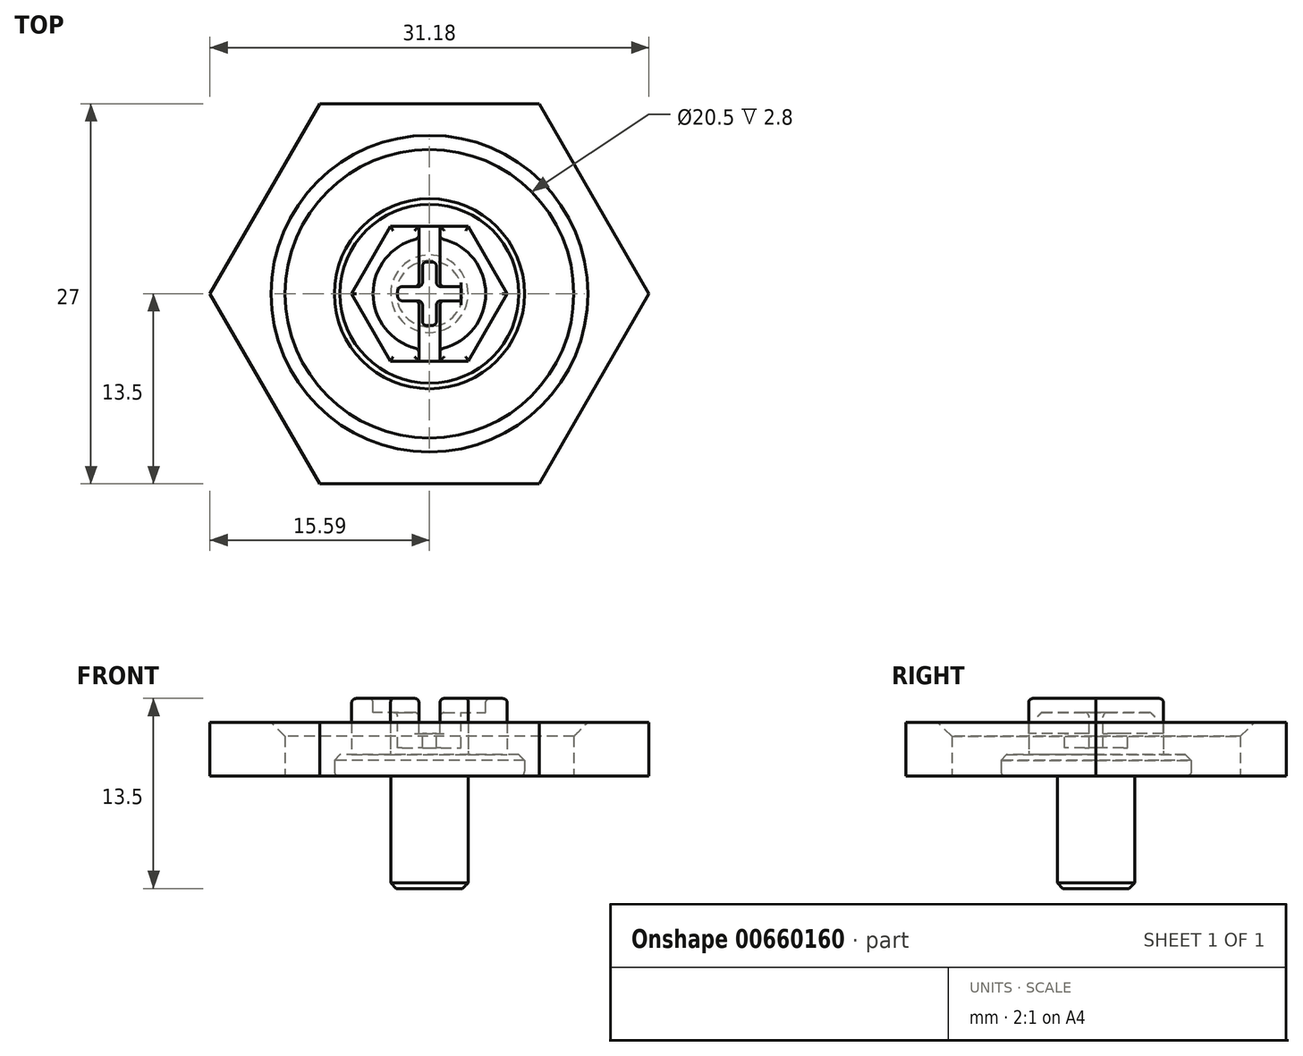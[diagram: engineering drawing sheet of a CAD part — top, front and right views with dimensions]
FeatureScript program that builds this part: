
annotation { "Feature Type Name" : "Feature", "Feature Type Description" : "" }
export const myFeature = defineFeature(function(context is Context, id is Id, definition is map)
    precondition{}
    {
        {
            var Q0;
            Q0=qCreatedBy(makeId("Top.planeOp"),FACE);
            var sketch = newSketch(context, id + "F0", { "sketchPlane" : qUnion([Q0])});
            skCircle(sketch, "E0.cCircle", {"center": v(0, 0) * mm, "radius": 13.5 * mm, "construction": true});
            skLineSegment(sketch, "E0.0", {"start": v(-7.8, 13.5) * mm, "end": v(7.8, 13.5) * mm});
            skLineSegment(sketch, "E0.1", {"start": v(7.8, 13.5) * mm, "end": v(15.59, 0) * mm});
            skLineSegment(sketch, "E0.2", {"start": v(15.59, 0) * mm, "end": v(7.8, -13.5) * mm});
            skLineSegment(sketch, "E0.3", {"start": v(7.8, -13.5) * mm, "end": v(-7.8, -13.5) * mm});
            skLineSegment(sketch, "E0.4", {"start": v(-7.8, -13.5) * mm, "end": v(-15.59, 0) * mm});
            skLineSegment(sketch, "E0.5", {"start": v(-15.59, 0) * mm, "end": v(-7.8, 13.5) * mm});
            skPoint(sketch, "E0.0.midPoint", {"position": v(0, 13.5) * mm});
            skCircle(sketch, "E1", {"center": v(0, 0) * mm, "radius": 10.25 * mm});
            skSolve(sketch);
        }
        {
            var Q0;
            Q0=makeQuery(id+"F0.imprint","IMPRINT",FACE,{"disambiguationData":[TD([[makeQuery(id+"F0.imprint","IMPRINT",EDGE,{"derivedFrom":sQuery(id+"F0.wireOp",EDGE,"E0.0")}),-1.0]])]});
            extrude(context, id + "F1", {"entities" : qUnion([Q0]), "depth" : 3.8 * mm});
        }
        {
            var Q0;
            Q0=makeQuery(id+"F1.opExtrude","CAP_EDGE",EDGE,{"disambiguationData":[OSD([sQuery(id+"F0.wireOp",EDGE,"E1")])],"isStart":false});
            chamfer(context, id + "F2", {"entities" : qUnion([Q0]), "width" : 1 * mm, "tangentPropagation" : true});
        }
        {
            var Q0;
            Q0=qCreatedBy(makeId("Top.planeOp"),FACE);
            var sketch = newSketch(context, id + "F3", { "sketchPlane" : qUnion([Q0])});
            skCircle(sketch, "E2", {"center": v(0, 0) * mm, "radius": 6.75 * mm});
            skCircle(sketch, "E3", {"center": v(0, 0) * mm, "radius": 2.75 * mm});
            skSolve(sketch);
        }
        {
            var Q0;
            Q0=makeQuery(id+"F3.imprint","IMPRINT",FACE,{"disambiguationData":[TD([[makeQuery(id+"F3.imprint","IMPRINT",EDGE,{"derivedFrom":sQuery(id+"F3.wireOp",EDGE,"E3")}),1.0]])]});
            extrude(context, id + "F4", {"entities" : qUnion([Q0]), "oppositeDirection" : true, "depth" : 8 * mm});
        }
        {
            var Q0;
            Q0=makeQuery(id+"F3.imprint","IMPRINT",FACE,{"disambiguationData":[TD([[makeQuery(id+"F3.imprint","IMPRINT",EDGE,{"derivedFrom":sQuery(id+"F3.wireOp",EDGE,"E2")}),1.0]])]});
            var Q1;
            Q1=makeQuery(id+"F3.imprint","IMPRINT",FACE,{"disambiguationData":[TD([[makeQuery(id+"F3.imprint","IMPRINT",EDGE,{"derivedFrom":sQuery(id+"F3.wireOp",EDGE,"E3")}),1.0]])]});
            extrude(context, id + "F5", {"entities" : qUnion([Q0, Q1]), "operationType" : NewBodyOperationType.ADD, "depth" : 1.5 * mm});
        }
        {
            var Q0;
            Q0=makeQuery(id+"F5.opExtrude","CAP_FACE",FACE,{"disambiguationData":[OSD([sQuery(id+"F3.wireOp",EDGE,"E2")])],"isStart":false});
            var sketch = newSketch(context, id + "F6", { "sketchPlane" : qUnion([Q0])});
            skCircle(sketch, "E4.cCircle", {"center": v(0, 0) * mm, "radius": 4.78 * mm, "construction": true});
            skLineSegment(sketch, "E4.0", {"start": v(-2.76, 4.78) * mm, "end": v(2.76, 4.78) * mm});
            skLineSegment(sketch, "E4.1", {"start": v(2.76, 4.78) * mm, "end": v(5.53, 0) * mm});
            skLineSegment(sketch, "E4.2", {"start": v(5.53, 0) * mm, "end": v(2.76, -4.78) * mm});
            skLineSegment(sketch, "E4.3", {"start": v(2.76, -4.78) * mm, "end": v(-2.76, -4.78) * mm});
            skLineSegment(sketch, "E4.4", {"start": v(-2.76, -4.78) * mm, "end": v(-5.53, 0) * mm});
            skLineSegment(sketch, "E4.5", {"start": v(-5.53, 0) * mm, "end": v(-2.76, 4.78) * mm});
            skPoint(sketch, "E4.0.midPoint", {"position": v(0, 4.78) * mm});
            skSolve(sketch);
        }
        {
            var Q0;
            Q0=makeQuery(id+"F6.imprint","IMPRINT",FACE,{"disambiguationData":[TD([[makeQuery(id+"F6.imprint","IMPRINT",EDGE,{"derivedFrom":sQuery(id+"F6.wireOp",EDGE,"E4.0")}),-1.0]])]});
            extrude(context, id + "F7", {"entities" : qUnion([Q0]), "operationType" : NewBodyOperationType.ADD, "depth" : 4 * mm});
        }
        {
            var Q0;
            Q0=makeQuery(id+"F7.opExtrude","CAP_FACE",FACE,{"disambiguationData":[OSD([sQuery(id+"F6.wireOp",EDGE,"E4.0"),sQuery(id+"F6.wireOp",EDGE,"E4.1"),sQuery(id+"F6.wireOp",EDGE,"E4.2"),sQuery(id+"F6.wireOp",EDGE,"E4.3"),sQuery(id+"F6.wireOp",EDGE,"E4.4"),sQuery(id+"F6.wireOp",EDGE,"E4.5")])],"isStart":false});
            var sketch = newSketch(context, id + "F8", { "sketchPlane" : qUnion([Q0])});
            skCircle(sketch, "E5", {"center": v(0, 0) * mm, "radius": 4 * mm});
            skSolve(sketch);
        }
        {
            var Q0;
            Q0=makeQuery(id+"F8.imprint","IMPRINT",FACE,{"disambiguationData":[TD([[makeQuery(id+"F8.imprint","IMPRINT",EDGE,{"derivedFrom":sQuery(id+"F8.wireOp",EDGE,"E5")}),1.0]])]});
            extrude(context, id + "F9", {"entities" : qUnion([Q0]), "operationType" : NewBodyOperationType.REMOVE, "oppositeDirection" : true, "depth" : 1 * mm});
        }
        {
            var Q0;
            Q0=makeQuery(id+"F7.opExtrude","CAP_FACE",FACE,{"disambiguationData":[OSD([sQuery(id+"F6.wireOp",EDGE,"E4.0"),sQuery(id+"F6.wireOp",EDGE,"E4.1"),sQuery(id+"F6.wireOp",EDGE,"E4.2"),sQuery(id+"F6.wireOp",EDGE,"E4.3"),sQuery(id+"F6.wireOp",EDGE,"E4.4"),sQuery(id+"F6.wireOp",EDGE,"E4.5")])],"isStart":false});
            var sketch = newSketch(context, id + "F10", { "sketchPlane" : qUnion([Q0])});
            skLineSegment(sketch, "E6.bottom", {"start": v(-0.75, 5) * mm, "end": v(0.75, 5) * mm});
            skLineSegment(sketch, "E6.top", {"start": v(-0.75, -5) * mm, "end": v(0.75, -5) * mm});
            skLineSegment(sketch, "E6.left", {"start": v(-0.75, 5) * mm, "end": v(-0.75, -5) * mm});
            skLineSegment(sketch, "E6.right", {"start": v(0.75, 5) * mm, "end": v(0.75, -5) * mm});
            skPoint(sketch, "E6.middle", {"position": v(0, 0) * mm});
            skSolve(sketch);
        }
        {
            var Q0;
            {var subQ0=sQuery(id+"F10.wireOp",EDGE,"E6.left");var subQ1=makeQuery(id+"F7.opExtrude","CAP_EDGE",EDGE,{"disambiguationData":[OSD([sQuery(id+"F6.wireOp",EDGE,"E4.0")])],"isStart":false});var subQ2=makeQuery(id+"F10.imprint","INTERSECT",VERTEX,{"derivedFrom":[subQ1,subQ0]});Q0=makeQuery(id+"F10.imprint","IMPRINT",FACE,{"disambiguationData":[TD([[makeQuery(id+"F10.imprint","IMPRINT",EDGE,{"disambiguationData":[TD([[subQ2,-1.0]])],"derivedFrom":subQ0}),1.0]])]});}
            var Q1;
            {var subQ0=sQuery(id+"F10.wireOp",EDGE,"E6.left");var subQ1=makeQuery(id+"F9.boolean.opBoolean","COPY",EDGE,{"derivedFrom":makeQuery(id+"F9.opExtrude","CAP_EDGE",EDGE,{"disambiguationData":[OSD([sQuery(id+"F8.wireOp",EDGE,"E5")])],"isStart":true})});var subQ2=makeQuery(id+"F10.imprint","INTERSECT",VERTEX,{"disambiguationData":[OD(0.0)],"derivedFrom":[subQ1,subQ0]});Q1=makeQuery(id+"F10.imprint","IMPRINT",FACE,{"disambiguationData":[TD([[makeQuery(id+"F10.imprint","IMPRINT",EDGE,{"disambiguationData":[TD([[subQ2,-1.0]])],"derivedFrom":subQ0}),1.0]])]});}
            var Q2;
            {var subQ0=sQuery(id+"F10.wireOp",EDGE,"E6.left");var subQ1=makeQuery(id+"F7.opExtrude","CAP_EDGE",EDGE,{"disambiguationData":[OSD([sQuery(id+"F6.wireOp",EDGE,"E4.3")])],"isStart":false});var subQ2=makeQuery(id+"F10.imprint","INTERSECT",VERTEX,{"derivedFrom":[subQ1,subQ0]});Q2=makeQuery(id+"F10.imprint","IMPRINT",FACE,{"disambiguationData":[TD([[makeQuery(id+"F10.imprint","IMPRINT",EDGE,{"disambiguationData":[TD([[subQ2,1.0]])],"derivedFrom":subQ0}),1.0]])]});}
            var Q3;
            Q3=makeQuery(id+"F5.opExtrude","CAP_FACE",FACE,{"disambiguationData":[OSD([sQuery(id+"F3.wireOp",EDGE,"E2")])],"isStart":false});
            extrude(context, id + "F11", {"entities" : qUnion([Q0, Q1, Q2]), "operationType" : NewBodyOperationType.REMOVE, "oppositeDirection" : true, "endBoundEntityFace" : qUnion([Q3]), "depth" : 2.5 * mm});
        }
        {
            var Q0;
            {var subQ0=sQuery(id+"F8.wireOp",EDGE,"E5");Q0=makeQuery(id+"F11.boolean.opBoolean","SPLIT",FACE,{"disambiguationData":[TD([makeQuery(id+"F11.opExtrude","SWEPT_FACE",FACE,{"disambiguationData":[OSD([sQuery(id+"F10.wireOp",EDGE,"E6.left")])]})])],"derivedFrom":makeQuery(id+"F9.boolean.opBoolean","COPY",FACE,{"derivedFrom":makeQuery(id+"F9.opExtrude","CAP_FACE",FACE,{"disambiguationData":[OSD([subQ0])],"isStart":false})})});}
            var sketch = newSketch(context, id + "F12", { "sketchPlane" : qUnion([Q0])});
            skLineSegment(sketch, "E7.bottom", {"start": v(-0.5, 2.25) * mm, "end": v(0.5, 2.25) * mm});
            skLineSegment(sketch, "E7.top", {"start": v(-0.5, -2.25) * mm, "end": v(0.5, -2.25) * mm});
            skLineSegment(sketch, "E7.left", {"start": v(-0.5, 2.25) * mm, "end": v(-0.5, -2.25) * mm});
            skLineSegment(sketch, "E7.right", {"start": v(0.5, 2.25) * mm, "end": v(0.5, -2.25) * mm});
            skPoint(sketch, "E7.middle", {"position": v(0, 0) * mm});
            skLineSegment(sketch, "E8.bottom", {"start": v(-2.25, 0.5) * mm, "end": v(2.25, 0.5) * mm});
            skLineSegment(sketch, "E8.top", {"start": v(-2.25, -0.5) * mm, "end": v(2.25, -0.5) * mm});
            skLineSegment(sketch, "E8.left", {"start": v(-2.25, 0.5) * mm, "end": v(-2.25, -0.5) * mm});
            skLineSegment(sketch, "E8.right", {"start": v(2.25, 0.5) * mm, "end": v(2.25, -0.5) * mm});
            skSolve(sketch);
        }
        {
            var Q0;
            {var subQ5=sQuery(id+"F12.wireOp",EDGE,"E8.right");Q0=makeQuery(id+"F12.imprint","IMPRINT",FACE,{"disambiguationData":[TD([[makeQuery(id+"F12.imprint","IMPRINT",EDGE,{"derivedFrom":subQ5}),-1.0]])]});}
            var Q1;
            {var subQ0=sQuery(id+"F12.wireOp",EDGE,"E8.bottom");var subQ1=sQuery(id+"F12.wireOp",EDGE,"E7.left");var subQ2=makeQuery(id+"F12.imprint","INTERSECT",VERTEX,{"derivedFrom":[subQ1,subQ0]});Q1=makeQuery(id+"F12.imprint","IMPRINT",FACE,{"disambiguationData":[TD([[makeQuery(id+"F12.imprint","IMPRINT",EDGE,{"disambiguationData":[TD([[subQ2,-1.0]])],"derivedFrom":subQ1}),1.0]])]});}
            var Q2;
            {var subQ0=sQuery(id+"F12.wireOp",EDGE,"E7.bottom");Q2=makeQuery(id+"F12.imprint","IMPRINT",FACE,{"disambiguationData":[TD([[makeQuery(id+"F12.imprint","IMPRINT",EDGE,{"derivedFrom":subQ0}),-1.0]])]});}
            var Q3;
            {var subQ0=sQuery(id+"F12.wireOp",EDGE,"E7.top");Q3=makeQuery(id+"F12.imprint","IMPRINT",FACE,{"disambiguationData":[TD([[makeQuery(id+"F12.imprint","IMPRINT",EDGE,{"derivedFrom":subQ0}),1.0]])]});}
            var Q4;
            {var subQ0=sQuery(id+"F12.wireOp",EDGE,"E8.left");Q4=makeQuery(id+"F12.imprint","IMPRINT",FACE,{"disambiguationData":[TD([[makeQuery(id+"F12.imprint","IMPRINT",EDGE,{"derivedFrom":subQ0}),1.0]])]});}
            var Q5;
            {var subQ0=sQuery(id+"F12.wireOp",EDGE,"E8.bottom");var subQ1=sQuery(id+"F12.wireOp",EDGE,"E7.left");var subQ2=makeQuery(id+"F12.imprint","INTERSECT",VERTEX,{"derivedFrom":[subQ1,subQ0]});Q5=makeQuery(id+"F12.imprint","IMPRINT",FACE,{"disambiguationData":[TD([[makeQuery(id+"F12.imprint","IMPRINT",EDGE,{"disambiguationData":[TD([[subQ2,-1.0]])],"derivedFrom":subQ1}),-1.0]])]});}
            extrude(context, id + "F13", {"entities" : qUnion([Q0, Q1, Q2, Q3, Q4, Q5]), "operationType" : NewBodyOperationType.REMOVE, "oppositeDirection" : true, "depth" : 2.5 * mm});
        }
        {
            var Q0;
            {var subQ0=sQuery(id+"F6.wireOp",EDGE,"E4.5");var subQ1=sQuery(id+"F6.wireOp",EDGE,"E4.4");var subQ2=sQuery(id+"F6.wireOp",EDGE,"E4.3");var subQ3=sQuery(id+"F6.wireOp",EDGE,"E4.0");Q0=makeQuery(id+"F11.boolean.opBoolean","SPLIT",FACE,{"disambiguationData":[TD([makeQuery(id+"F7.opExtrude","SWEPT_FACE",FACE,{"disambiguationData":[OSD([subQ1])]})])],"derivedFrom":makeQuery(id+"F7.opExtrude","CAP_FACE",FACE,{"disambiguationData":[OSD([subQ3,sQuery(id+"F6.wireOp",EDGE,"E4.1"),sQuery(id+"F6.wireOp",EDGE,"E4.2"),subQ2,subQ1,subQ0])],"isStart":false})});}
            var Q1;
            {var subQ0=sQuery(id+"F6.wireOp",EDGE,"E4.2");var subQ1=sQuery(id+"F6.wireOp",EDGE,"E4.1");var subQ2=sQuery(id+"F6.wireOp",EDGE,"E4.3");var subQ3=sQuery(id+"F6.wireOp",EDGE,"E4.0");Q1=makeQuery(id+"F11.boolean.opBoolean","SPLIT",FACE,{"disambiguationData":[TD([makeQuery(id+"F7.opExtrude","SWEPT_FACE",FACE,{"disambiguationData":[OSD([subQ1])]})])],"derivedFrom":makeQuery(id+"F7.opExtrude","CAP_FACE",FACE,{"disambiguationData":[OSD([subQ3,subQ1,subQ0,subQ2,sQuery(id+"F6.wireOp",EDGE,"E4.4"),sQuery(id+"F6.wireOp",EDGE,"E4.5")])],"isStart":false})});}
            var Q2;
            Q2=makeQuery(id+"F11.boolean.opBoolean","COPY",EDGE,{"derivedFrom":makeQuery(id+"F11.opExtrude","SWEPT_EDGE",EDGE,{"disambiguationData":[OSD([sQuery(id+"F6.wireOp",EDGE,"E4.3"),sQuery(id+"F10.wireOp",EDGE,"E6.left")])]})});
            var Q3;
            Q3=makeQuery(id+"F11.boolean.opBoolean","COPY",EDGE,{"derivedFrom":makeQuery(id+"F11.opExtrude","CAP_EDGE",EDGE,{"disambiguationData":[OSD([sQuery(id+"F6.wireOp",EDGE,"E4.3")])],"isStart":false})});
            var Q4;
            Q4=makeQuery(id+"F11.boolean.opBoolean","COPY",EDGE,{"derivedFrom":makeQuery(id+"F11.opExtrude","SWEPT_EDGE",EDGE,{"disambiguationData":[OSD([sQuery(id+"F6.wireOp",EDGE,"E4.3"),sQuery(id+"F10.wireOp",EDGE,"E6.right")])]})});
            var Q5;
            Q5=makeQuery(id+"F11.boolean.opBoolean","COPY",EDGE,{"derivedFrom":makeQuery(id+"F11.opExtrude","SWEPT_EDGE",EDGE,{"disambiguationData":[OSD([sQuery(id+"F6.wireOp",EDGE,"E4.0"),sQuery(id+"F10.wireOp",EDGE,"E6.left")])]})});
            var Q6;
            Q6=makeQuery(id+"F11.boolean.opBoolean","COPY",EDGE,{"derivedFrom":makeQuery(id+"F11.opExtrude","CAP_EDGE",EDGE,{"disambiguationData":[OSD([sQuery(id+"F6.wireOp",EDGE,"E4.0")])],"isStart":false})});
            var Q7;
            Q7=makeQuery(id+"F11.boolean.opBoolean","COPY",EDGE,{"derivedFrom":makeQuery(id+"F11.opExtrude","SWEPT_EDGE",EDGE,{"disambiguationData":[OSD([sQuery(id+"F6.wireOp",EDGE,"E4.0"),sQuery(id+"F10.wireOp",EDGE,"E6.right")])]})});
            var Q8;
            {var subQ0=sQuery(id+"F8.wireOp",EDGE,"E5");var subQ1=makeQuery(id+"F9.boolean.opBoolean","COPY",FACE,{"derivedFrom":makeQuery(id+"F9.opExtrude","CAP_FACE",FACE,{"disambiguationData":[OSD([subQ0])],"isStart":false})});var subQ2=makeQuery(id+"F11.opExtrude","SWEPT_FACE",FACE,{"disambiguationData":[OSD([sQuery(id+"F10.wireOp",EDGE,"E6.right")])]});var subQ3=sQuery(id+"F12.wireOp",EDGE,"E8.top");Q8=makeQuery(id+"F13.boolean.opBoolean","SPLIT",EDGE,{"disambiguationData":[TD([makeQuery(id+"F13.opExtrude","SWEPT_FACE",FACE,{"disambiguationData":[OSD([subQ3]),TDD([makeQuery(id+"F12.imprint","IMPRINT",EDGE,{"disambiguationData":[TD([[makeQuery(id+"F12.imprint","INTERSECT",VERTEX,{"derivedFrom":[subQ3,sQuery(id+"F12.wireOp",EDGE,"E8.right")]}),1.0]])],"derivedFrom":subQ3})])]})])],"derivedFrom":makeQuery(id+"F11.boolean.opBoolean","INTERSECT",EDGE,{"derivedFrom":[subQ1,subQ2]})});}
            var Q9;
            {var subQ0=sQuery(id+"F8.wireOp",EDGE,"E5");var subQ1=makeQuery(id+"F9.boolean.opBoolean","COPY",FACE,{"derivedFrom":makeQuery(id+"F9.opExtrude","CAP_FACE",FACE,{"disambiguationData":[OSD([subQ0])],"isStart":false})});var subQ2=makeQuery(id+"F11.opExtrude","SWEPT_FACE",FACE,{"disambiguationData":[OSD([sQuery(id+"F10.wireOp",EDGE,"E6.right")])]});var subQ3=sQuery(id+"F12.wireOp",EDGE,"E8.bottom");Q9=makeQuery(id+"F13.boolean.opBoolean","SPLIT",EDGE,{"disambiguationData":[TD([makeQuery(id+"F13.opExtrude","SWEPT_FACE",FACE,{"disambiguationData":[OSD([subQ3]),TDD([makeQuery(id+"F12.imprint","IMPRINT",EDGE,{"disambiguationData":[TD([[makeQuery(id+"F12.imprint","INTERSECT",VERTEX,{"derivedFrom":[subQ3,sQuery(id+"F12.wireOp",EDGE,"E8.right")]}),1.0]])],"derivedFrom":subQ3})])]})])],"derivedFrom":makeQuery(id+"F11.boolean.opBoolean","INTERSECT",EDGE,{"derivedFrom":[subQ1,subQ2]})});}
            var Q10;
            Q10=makeQuery(id+"F11.boolean.opBoolean","INTERSECT",EDGE,{"disambiguationData":[OD(0.0)],"derivedFrom":[makeQuery(id+"F9.boolean.opBoolean","COPY",FACE,{"derivedFrom":makeQuery(id+"F9.opExtrude","SWEPT_FACE",FACE,{"disambiguationData":[OSD([sQuery(id+"F8.wireOp",EDGE,"E5")])]})}),makeQuery(id+"F11.opExtrude","SWEPT_FACE",FACE,{"disambiguationData":[OSD([sQuery(id+"F10.wireOp",EDGE,"E6.right")])]})]});
            var Q11;
            {var subQ0=sQuery(id+"F12.wireOp",EDGE,"E8.bottom");Q11=makeQuery(id+"F13.boolean.opBoolean","COPY",EDGE,{"derivedFrom":makeQuery(id+"F13.opExtrude","CAP_EDGE",EDGE,{"disambiguationData":[OSD([subQ0]),TDD([makeQuery(id+"F12.imprint","IMPRINT",EDGE,{"disambiguationData":[TD([[makeQuery(id+"F12.imprint","INTERSECT",VERTEX,{"derivedFrom":[subQ0,sQuery(id+"F12.wireOp",EDGE,"E8.right")]}),1.0]])],"derivedFrom":subQ0})])],"isStart":true})});}
            var Q12;
            Q12=makeQuery(id+"F13.boolean.opBoolean","COPY",EDGE,{"derivedFrom":makeQuery(id+"F13.opExtrude","CAP_EDGE",EDGE,{"disambiguationData":[OSD([sQuery(id+"F12.wireOp",EDGE,"E8.right")])],"isStart":true})});
            var Q13;
            {var subQ0=sQuery(id+"F12.wireOp",EDGE,"E8.top");Q13=makeQuery(id+"F13.boolean.opBoolean","COPY",EDGE,{"derivedFrom":makeQuery(id+"F13.opExtrude","CAP_EDGE",EDGE,{"disambiguationData":[OSD([subQ0]),TDD([makeQuery(id+"F12.imprint","IMPRINT",EDGE,{"disambiguationData":[TD([[makeQuery(id+"F12.imprint","INTERSECT",VERTEX,{"derivedFrom":[subQ0,sQuery(id+"F12.wireOp",EDGE,"E8.right")]}),1.0]])],"derivedFrom":subQ0})])],"isStart":true})});}
            var Q14;
            Q14=makeQuery(id+"F11.boolean.opBoolean","INTERSECT",EDGE,{"disambiguationData":[OD(1.0)],"derivedFrom":[makeQuery(id+"F9.boolean.opBoolean","COPY",FACE,{"derivedFrom":makeQuery(id+"F9.opExtrude","SWEPT_FACE",FACE,{"disambiguationData":[OSD([sQuery(id+"F8.wireOp",EDGE,"E5")])]})}),makeQuery(id+"F11.opExtrude","SWEPT_FACE",FACE,{"disambiguationData":[OSD([sQuery(id+"F10.wireOp",EDGE,"E6.right")])]})]});
            var Q15;
            Q15=makeQuery(id+"F11.boolean.opBoolean","INTERSECT",EDGE,{"disambiguationData":[OD(1.0)],"derivedFrom":[makeQuery(id+"F9.boolean.opBoolean","COPY",FACE,{"derivedFrom":makeQuery(id+"F9.opExtrude","SWEPT_FACE",FACE,{"disambiguationData":[OSD([sQuery(id+"F8.wireOp",EDGE,"E5")])]})}),makeQuery(id+"F11.opExtrude","SWEPT_FACE",FACE,{"disambiguationData":[OSD([sQuery(id+"F10.wireOp",EDGE,"E6.left")])]})]});
            var Q16;
            {var subQ0=sQuery(id+"F8.wireOp",EDGE,"E5");var subQ1=makeQuery(id+"F9.boolean.opBoolean","COPY",FACE,{"derivedFrom":makeQuery(id+"F9.opExtrude","CAP_FACE",FACE,{"disambiguationData":[OSD([subQ0])],"isStart":false})});var subQ2=makeQuery(id+"F11.opExtrude","SWEPT_FACE",FACE,{"disambiguationData":[OSD([sQuery(id+"F10.wireOp",EDGE,"E6.left")])]});var subQ3=sQuery(id+"F12.wireOp",EDGE,"E8.top");var subQ4=makeQuery(id+"F11.boolean.opBoolean","INTERSECT",EDGE,{"derivedFrom":[subQ1,subQ2]});Q16=makeQuery(id+"F13.boolean.opBoolean","SPLIT",EDGE,{"disambiguationData":[TD([makeQuery(id+"F13.opExtrude","SWEPT_FACE",FACE,{"disambiguationData":[OSD([subQ3]),TDD([makeQuery(id+"F12.imprint","IMPRINT",EDGE,{"disambiguationData":[TD([[makeQuery(id+"F12.imprint","INTERSECT",VERTEX,{"derivedFrom":[subQ3,sQuery(id+"F12.wireOp",EDGE,"E8.left")]}),-1.0]])],"derivedFrom":subQ3}),makeQuery(id+"F12.imprint","IMPRINT",EDGE,{"disambiguationData":[TD([[makeQuery(id+"F12.imprint","INTERSECT",VERTEX,{"derivedFrom":[sQuery(id+"F12.wireOp",EDGE,"E7.left"),subQ3]}),1.0]])],"derivedFrom":subQ3})])]})])],"derivedFrom":subQ4});}
            var Q17;
            {var subQ0=sQuery(id+"F12.wireOp",EDGE,"E8.top");Q17=makeQuery(id+"F13.boolean.opBoolean","COPY",EDGE,{"derivedFrom":makeQuery(id+"F13.opExtrude","CAP_EDGE",EDGE,{"disambiguationData":[OSD([subQ0]),TDD([makeQuery(id+"F12.imprint","IMPRINT",EDGE,{"disambiguationData":[TD([[makeQuery(id+"F12.imprint","INTERSECT",VERTEX,{"derivedFrom":[subQ0,sQuery(id+"F12.wireOp",EDGE,"E8.left")]}),-1.0]])],"derivedFrom":subQ0}),makeQuery(id+"F12.imprint","IMPRINT",EDGE,{"disambiguationData":[TD([[makeQuery(id+"F12.imprint","INTERSECT",VERTEX,{"derivedFrom":[sQuery(id+"F12.wireOp",EDGE,"E7.left"),subQ0]}),1.0]])],"derivedFrom":subQ0})])],"isStart":true})});}
            var Q18;
            {var subQ0=sQuery(id+"F12.wireOp",EDGE,"E8.bottom");Q18=makeQuery(id+"F13.boolean.opBoolean","COPY",EDGE,{"derivedFrom":makeQuery(id+"F13.opExtrude","CAP_EDGE",EDGE,{"disambiguationData":[OSD([subQ0]),TDD([makeQuery(id+"F12.imprint","IMPRINT",EDGE,{"disambiguationData":[TD([[makeQuery(id+"F12.imprint","INTERSECT",VERTEX,{"derivedFrom":[subQ0,sQuery(id+"F12.wireOp",EDGE,"E8.left")]}),-1.0]])],"derivedFrom":subQ0}),makeQuery(id+"F12.imprint","IMPRINT",EDGE,{"disambiguationData":[TD([[makeQuery(id+"F12.imprint","INTERSECT",VERTEX,{"derivedFrom":[sQuery(id+"F12.wireOp",EDGE,"E7.left"),subQ0]}),1.0]])],"derivedFrom":subQ0})])],"isStart":true})});}
            var Q19;
            Q19=makeQuery(id+"F13.boolean.opBoolean","COPY",EDGE,{"derivedFrom":makeQuery(id+"F13.opExtrude","CAP_EDGE",EDGE,{"disambiguationData":[OSD([sQuery(id+"F12.wireOp",EDGE,"E8.left")])],"isStart":true})});
            var Q20;
            {var subQ0=sQuery(id+"F8.wireOp",EDGE,"E5");var subQ1=sQuery(id+"F12.wireOp",EDGE,"E8.bottom");var subQ2=makeQuery(id+"F11.opExtrude","SWEPT_FACE",FACE,{"disambiguationData":[OSD([sQuery(id+"F10.wireOp",EDGE,"E6.left")])]});var subQ3=makeQuery(id+"F9.boolean.opBoolean","COPY",FACE,{"derivedFrom":makeQuery(id+"F9.opExtrude","CAP_FACE",FACE,{"disambiguationData":[OSD([subQ0])],"isStart":false})});var subQ4=makeQuery(id+"F11.boolean.opBoolean","INTERSECT",EDGE,{"derivedFrom":[subQ3,subQ2]});Q20=makeQuery(id+"F13.boolean.opBoolean","SPLIT",EDGE,{"disambiguationData":[TD([makeQuery(id+"F13.opExtrude","SWEPT_FACE",FACE,{"disambiguationData":[OSD([subQ1]),TDD([makeQuery(id+"F12.imprint","IMPRINT",EDGE,{"disambiguationData":[TD([[makeQuery(id+"F12.imprint","INTERSECT",VERTEX,{"derivedFrom":[subQ1,sQuery(id+"F12.wireOp",EDGE,"E8.left")]}),-1.0]])],"derivedFrom":subQ1}),makeQuery(id+"F12.imprint","IMPRINT",EDGE,{"disambiguationData":[TD([[makeQuery(id+"F12.imprint","INTERSECT",VERTEX,{"derivedFrom":[sQuery(id+"F12.wireOp",EDGE,"E7.left"),subQ1]}),1.0]])],"derivedFrom":subQ1})])]})])],"derivedFrom":subQ4});}
            var Q21;
            Q21=makeQuery(id+"F11.boolean.opBoolean","INTERSECT",EDGE,{"disambiguationData":[OD(0.0)],"derivedFrom":[makeQuery(id+"F9.boolean.opBoolean","COPY",FACE,{"derivedFrom":makeQuery(id+"F9.opExtrude","SWEPT_FACE",FACE,{"disambiguationData":[OSD([sQuery(id+"F8.wireOp",EDGE,"E5")])]})}),makeQuery(id+"F11.opExtrude","SWEPT_FACE",FACE,{"disambiguationData":[OSD([sQuery(id+"F10.wireOp",EDGE,"E6.left")])]})]});
            var Q22;
            Q22=makeQuery(id+"F13.boolean.opBoolean","COPY",EDGE,{"derivedFrom":makeQuery(id+"F13.opExtrude","SWEPT_EDGE",EDGE,{"disambiguationData":[OSD([sQuery(id+"F12.wireOp",EDGE,"E7.bottom"),sQuery(id+"F12.wireOp",EDGE,"E7.left")])]})});
            var Q23;
            Q23=makeQuery(id+"F13.boolean.opBoolean","COPY",EDGE,{"derivedFrom":makeQuery(id+"F13.opExtrude","SWEPT_EDGE",EDGE,{"disambiguationData":[OSD([sQuery(id+"F12.wireOp",EDGE,"E7.bottom"),sQuery(id+"F12.wireOp",EDGE,"E7.right")])]})});
            var Q24;
            Q24=makeQuery(id+"F13.boolean.opBoolean","COPY",EDGE,{"derivedFrom":makeQuery(id+"F13.opExtrude","SWEPT_EDGE",EDGE,{"disambiguationData":[OSD([sQuery(id+"F12.wireOp",EDGE,"E7.top"),sQuery(id+"F12.wireOp",EDGE,"E7.right")])]})});
            var Q25;
            Q25=makeQuery(id+"F13.boolean.opBoolean","COPY",EDGE,{"derivedFrom":makeQuery(id+"F13.opExtrude","SWEPT_EDGE",EDGE,{"disambiguationData":[OSD([sQuery(id+"F12.wireOp",EDGE,"E7.top"),sQuery(id+"F12.wireOp",EDGE,"E7.left")])]})});
            var Q26;
            Q26=makeQuery(id+"F13.boolean.opBoolean","COPY",EDGE,{"derivedFrom":makeQuery(id+"F13.opExtrude","SWEPT_EDGE",EDGE,{"disambiguationData":[OSD([sQuery(id+"F12.wireOp",EDGE,"E8.top"),sQuery(id+"F12.wireOp",EDGE,"E8.left")])]})});
            var Q27;
            Q27=makeQuery(id+"F13.boolean.opBoolean","COPY",EDGE,{"derivedFrom":makeQuery(id+"F13.opExtrude","SWEPT_EDGE",EDGE,{"disambiguationData":[OSD([sQuery(id+"F12.wireOp",EDGE,"E8.bottom"),sQuery(id+"F12.wireOp",EDGE,"E8.left")])]})});
            fillet(context, id + "F14", {"entities" : qUnion([Q0, Q1, Q2, Q3, Q4, Q5, Q6, Q7, Q8, Q9, Q10, Q11, Q12, Q13, Q14, Q15, Q16, Q17, Q18, Q19, Q20, Q21, Q22, Q23, Q24, Q25, Q26, Q27]), "radius" : .3 * mm, "tangentPropagation" : true, "allowEdgeOverflow" : false});
        }
        {
            var Q0;
            {var subQ0=sQuery(id+"F12.wireOp",EDGE,"E8.top");Q0=makeQuery(id+"F13.boolean.opBoolean","INTERSECT",EDGE,{"derivedFrom":[makeQuery(id+"F11.boolean.opBoolean","COPY",FACE,{"derivedFrom":makeQuery(id+"F11.opExtrude","SWEPT_FACE",FACE,{"disambiguationData":[OSD([sQuery(id+"F10.wireOp",EDGE,"E6.right")])]})}),makeQuery(id+"F13.opExtrude","SWEPT_FACE",FACE,{"disambiguationData":[OSD([subQ0]),TDD([makeQuery(id+"F12.imprint","IMPRINT",EDGE,{"disambiguationData":[TD([[makeQuery(id+"F12.imprint","INTERSECT",VERTEX,{"derivedFrom":[subQ0,sQuery(id+"F12.wireOp",EDGE,"E8.right")]}),1.0]])],"derivedFrom":subQ0})])]})]});}
            var Q1;
            {var subQ0=sQuery(id+"F12.wireOp",EDGE,"E8.bottom");Q1=makeQuery(id+"F13.boolean.opBoolean","INTERSECT",EDGE,{"derivedFrom":[makeQuery(id+"F11.boolean.opBoolean","COPY",FACE,{"derivedFrom":makeQuery(id+"F11.opExtrude","SWEPT_FACE",FACE,{"disambiguationData":[OSD([sQuery(id+"F10.wireOp",EDGE,"E6.right")])]})}),makeQuery(id+"F13.opExtrude","SWEPT_FACE",FACE,{"disambiguationData":[OSD([subQ0]),TDD([makeQuery(id+"F12.imprint","IMPRINT",EDGE,{"disambiguationData":[TD([[makeQuery(id+"F12.imprint","INTERSECT",VERTEX,{"derivedFrom":[subQ0,sQuery(id+"F12.wireOp",EDGE,"E8.right")]}),1.0]])],"derivedFrom":subQ0})])]})]});}
            var Q2;
            {var subQ0=sQuery(id+"F12.wireOp",EDGE,"E8.bottom");var subQ1=makeQuery(id+"F11.opExtrude","SWEPT_FACE",FACE,{"disambiguationData":[OSD([sQuery(id+"F10.wireOp",EDGE,"E6.left")])]});Q2=makeQuery(id+"F13.boolean.opBoolean","INTERSECT",EDGE,{"derivedFrom":[makeQuery(id+"F11.boolean.opBoolean","COPY",FACE,{"derivedFrom":subQ1}),makeQuery(id+"F13.opExtrude","SWEPT_FACE",FACE,{"disambiguationData":[OSD([subQ0]),TDD([makeQuery(id+"F12.imprint","IMPRINT",EDGE,{"disambiguationData":[TD([[makeQuery(id+"F12.imprint","INTERSECT",VERTEX,{"derivedFrom":[subQ0,sQuery(id+"F12.wireOp",EDGE,"E8.left")]}),-1.0]])],"derivedFrom":subQ0}),makeQuery(id+"F12.imprint","IMPRINT",EDGE,{"disambiguationData":[TD([[makeQuery(id+"F12.imprint","INTERSECT",VERTEX,{"derivedFrom":[sQuery(id+"F12.wireOp",EDGE,"E7.left"),subQ0]}),1.0]])],"derivedFrom":subQ0})])]})]});}
            var Q3;
            {var subQ0=sQuery(id+"F12.wireOp",EDGE,"E8.top");var subQ1=makeQuery(id+"F11.opExtrude","SWEPT_FACE",FACE,{"disambiguationData":[OSD([sQuery(id+"F10.wireOp",EDGE,"E6.left")])]});Q3=makeQuery(id+"F13.boolean.opBoolean","INTERSECT",EDGE,{"derivedFrom":[makeQuery(id+"F11.boolean.opBoolean","COPY",FACE,{"derivedFrom":subQ1}),makeQuery(id+"F13.opExtrude","SWEPT_FACE",FACE,{"disambiguationData":[OSD([subQ0]),TDD([makeQuery(id+"F12.imprint","IMPRINT",EDGE,{"disambiguationData":[TD([[makeQuery(id+"F12.imprint","INTERSECT",VERTEX,{"derivedFrom":[subQ0,sQuery(id+"F12.wireOp",EDGE,"E8.left")]}),-1.0]])],"derivedFrom":subQ0}),makeQuery(id+"F12.imprint","IMPRINT",EDGE,{"disambiguationData":[TD([[makeQuery(id+"F12.imprint","INTERSECT",VERTEX,{"derivedFrom":[sQuery(id+"F12.wireOp",EDGE,"E7.left"),subQ0]}),1.0]])],"derivedFrom":subQ0})])]})]});}
            fillet(context, id + "F15", {"entities" : qUnion([Q0, Q1, Q2, Q3]), "radius" : .3 * mm, "tangentPropagation" : true, "allowEdgeOverflow" : false});
        }
        {
            var Q0;
            Q0=makeQuery(id+"F13.boolean.opBoolean","COPY",EDGE,{"derivedFrom":makeQuery(id+"F13.opExtrude","SWEPT_EDGE",EDGE,{"disambiguationData":[OSD([sQuery(id+"F12.wireOp",EDGE,"E7.right"),sQuery(id+"F12.wireOp",EDGE,"E8.bottom")])]})});
            var Q1;
            Q1=makeQuery(id+"F13.boolean.opBoolean","COPY",EDGE,{"derivedFrom":makeQuery(id+"F13.opExtrude","SWEPT_EDGE",EDGE,{"disambiguationData":[OSD([sQuery(id+"F12.wireOp",EDGE,"E7.left"),sQuery(id+"F12.wireOp",EDGE,"E8.bottom")])]})});
            var Q2;
            Q2=makeQuery(id+"F13.boolean.opBoolean","COPY",EDGE,{"derivedFrom":makeQuery(id+"F13.opExtrude","SWEPT_EDGE",EDGE,{"disambiguationData":[OSD([sQuery(id+"F12.wireOp",EDGE,"E7.left"),sQuery(id+"F12.wireOp",EDGE,"E8.top")])]})});
            var Q3;
            Q3=makeQuery(id+"F13.boolean.opBoolean","COPY",EDGE,{"derivedFrom":makeQuery(id+"F13.opExtrude","SWEPT_EDGE",EDGE,{"disambiguationData":[OSD([sQuery(id+"F12.wireOp",EDGE,"E7.right"),sQuery(id+"F12.wireOp",EDGE,"E8.top")])]})});
            var Q4;
            Q4=makeQuery(id+"F5.opExtrude","CAP_EDGE",EDGE,{"disambiguationData":[OSD([sQuery(id+"F3.wireOp",EDGE,"E2")])],"isStart":true});
            fillet(context, id + "F16", {"entities" : qUnion([Q0, Q1, Q2, Q3, Q4]), "radius" : .3 * mm, "tangentPropagation" : true, "allowEdgeOverflow" : false});
        }
        {
            var Q0;
            Q0=makeQuery(id+"F5.opExtrude","CAP_EDGE",EDGE,{"disambiguationData":[OSD([sQuery(id+"F3.wireOp",EDGE,"E2")])],"isStart":false});
            var Q1;
            Q1=makeQuery(id+"F4.opExtrude","CAP_EDGE",EDGE,{"disambiguationData":[OSD([sQuery(id+"F3.wireOp",EDGE,"E3")])],"isStart":false});
            chamfer(context, id + "F17", {"entities" : qUnion([Q0, Q1]), "width" : .4 * mm, "tangentPropagation" : true});
        }
    });
